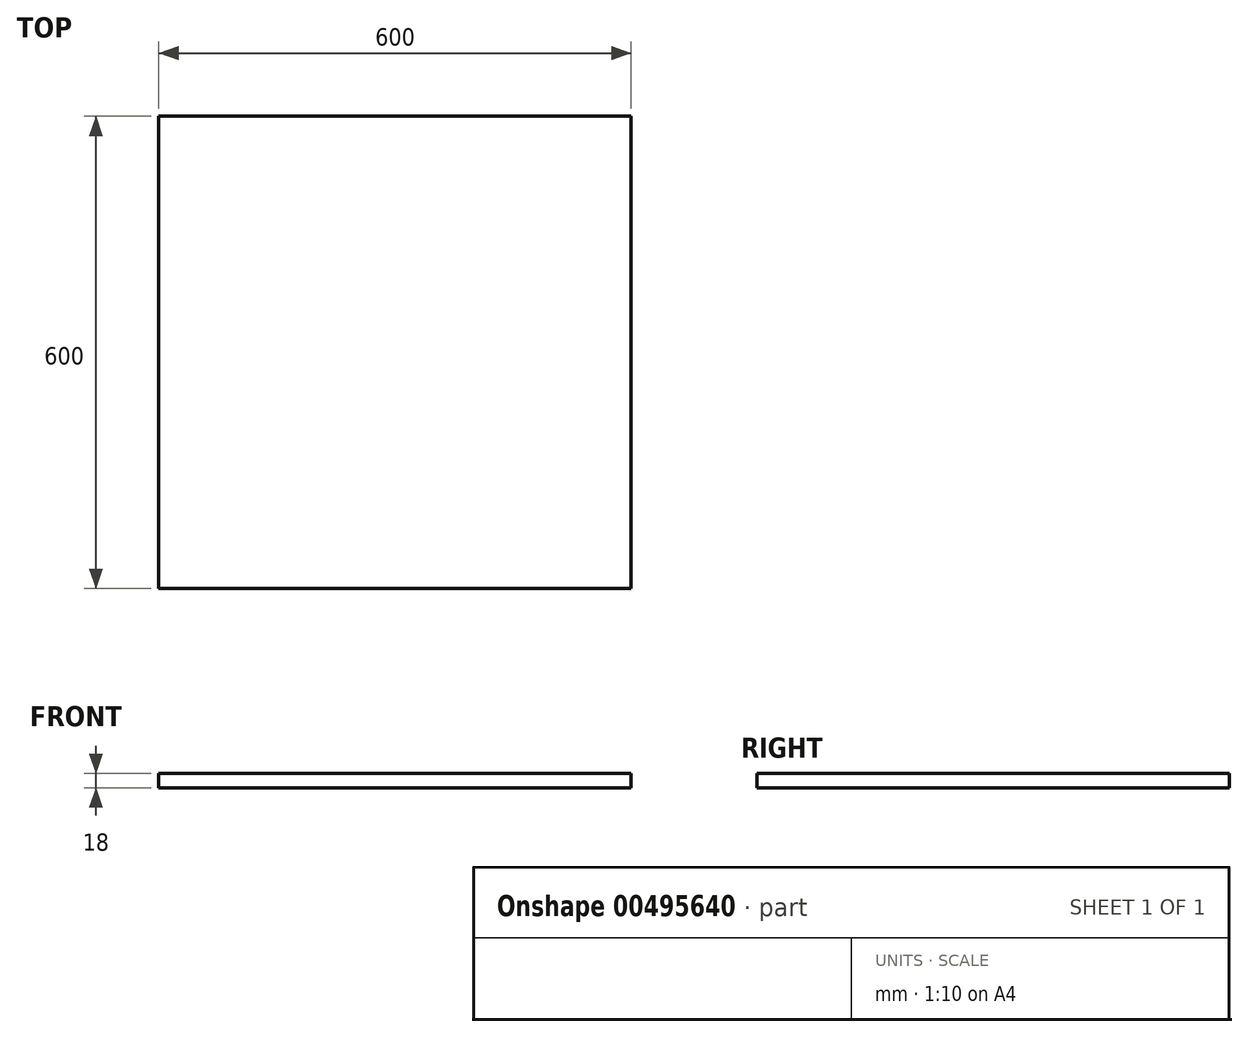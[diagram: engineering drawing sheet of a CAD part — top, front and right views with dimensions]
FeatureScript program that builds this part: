
annotation { "Feature Type Name" : "Feature", "Feature Type Description" : "" }
export const myFeature = defineFeature(function(context is Context, id is Id, definition is map)
    precondition{}
    {
        {
            var Q0;
            Q0=qCreatedBy(makeId("Front.planeOp"),FACE);
            var sketch = newSketch(context, id + "F0", { "sketchPlane" : qUnion([Q0])});
            skLineSegment(sketch, "E0.bottom", {"start": v(-291.71, 17.78) * mm, "end": v(308.29, 17.78) * mm});
            skLineSegment(sketch, "E0.top", {"start": v(-291.71, -0.22) * mm, "end": v(308.29, -0.22) * mm});
            skLineSegment(sketch, "E0.left", {"start": v(-291.71, 17.78) * mm, "end": v(-291.71, -0.22) * mm});
            skLineSegment(sketch, "E0.right", {"start": v(308.29, 17.78) * mm, "end": v(308.29, -0.22) * mm});
            skSolve(sketch);
        }
        {
            var Q0;
            Q0=makeQuery(id+"F0.imprint","IMPRINT",FACE,{"disambiguationData":[TD([[makeQuery(id+"F0.imprint","IMPRINT",EDGE,{"derivedFrom":sQuery(id+"F0.wireOp",EDGE,"E0.bottom")}),-1.0]])]});
            extrude(context, id + "F1", {"entities" : qUnion([Q0]), "oppositeDirection" : true, "depth" : 600 * mm});
        }
    });
